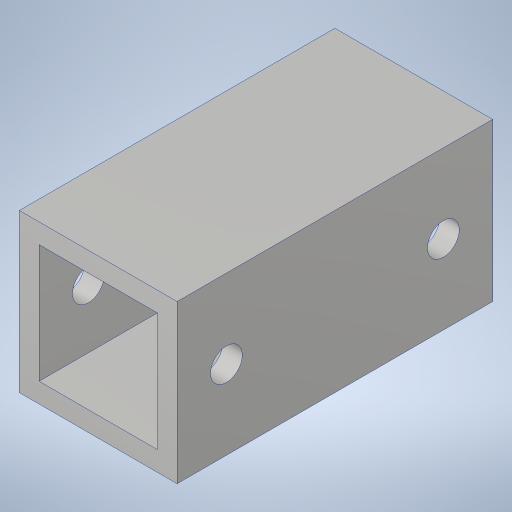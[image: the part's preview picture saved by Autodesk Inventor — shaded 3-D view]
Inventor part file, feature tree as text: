
AUTODESK INVENTOR PART (.ipt)
format: ipt  version: 2023.4 (Build 274418000, 418)  size: 212,992 bytes
history: native  units: in
note: dims shown in document units (in); Inventor stores cm internally (conversion verified against a paired STEP export)
features: extrude x1, hole x1, sketch x1
ambient origin geometry x8: Origin, YZ Plane, XZ Plane, XY Plane, X Axis, Y Axis, Z Axis, Center Point
bodies: Solid1 (feature_tree)
feature tree (3):
  extrude  "Extrusion1"  Depth=1.0in
  hole  "Hole2"  [1 undecoded]
  sketch  "Sketch3"  dims[d4=0.0in d22=1.375in d23=0.201in d24=0.75in d25=0.385in d26=0.25in d27=0.5635in d28=1.0in d29=0.8108in]
note: 1 required parameter value undecoded (feature->parameter linkage not recoverable at this tier; creation-order binding heuristic only, values carry confidence <= 0.55)
